# Revit family: Porta GBF
name_source: partatom
category: Doors
units: mm (PartAtom-declared; Revit-internal decimal feet)

## family parameters
Cut with Voids When Loaded = Yes
Host = Face
Room Calculation Point = No
Shared = No

## types (3) — shared parameters
Define Thermal Properties by = Schematic Type
zero-valued in all types: Default Elevation

## per-type parameters (varying)
| type | Altura Vao Luz | Espessura Folha | Height | Largura Vao Luz | Width |
| 70 - 800 x 1800 | 1800 mm  [stored 5.90551 ft] | 32 mm  [stored 0.104987 ft] | 1800 mm  [stored 5.90551 ft] | 800 mm  [stored 2.62467 ft] | 800 mm  [stored 2.62467 ft] |
| 150 - 1400 x 2200 | 2200 mm | 150 mm | 2200 mm | 1400 mm  [stored 4.59318 ft] | 1400 mm  [stored 4.59318 ft] |
| 100 - 1000 x 2100 | 2100 mm  [stored 6.88976 ft] | 32 mm  [stored 0.104987 ft] | 2100 mm  [stored 6.88976 ft] | 1000 mm  [stored 3.28084 ft] | 1000 mm  [stored 3.28084 ft] |

note: [stored X ft] marks values corroborated as IEEE doubles in the binary element streams (Revit-internal decimal feet)

## geometry (parser evidence)
native form markers: Blend x2
no freeform markers — native parametric forms only
